# Revit family: Centralini_in_lamiera_Bticino_da_incasso_porta_piena
name_source: partatom
category: Equipement électrique
revit_build: Autodesk Revit 2018 (Build: 20170223_1515(x64)
units: mm (PartAtom-declared; Revit-internal decimal feet)

## family parameters
Basée sur le plan de construction = Non
Configuration du panneau = Deux colonnes, circuits au sein
Cote de connecteur circulaire = Utiliser le diamètre
Couper avec des vides une fois chargée = Non
Numéro OmniClass = 23.80.30.11.17
Partagée = Non
Point de calcul de pièce = Non
Titre OmniClass = Distribution Boards and Control Panels
Toujours verticalement = Oui
Type d'élément = Tableau de raccordement

## types (6) — shared parameters
Colore = RAL 7035
Condizioni Generali di Utilizzo = https://export.legrand.com
Fabricant = bticino
IK = 08
IP = 30
URL = www.bticino.com
materia = metallo

## per-type parameters (varying)
| type | Altezza da incasso | E209P/12D | E209P/24D | E209P/36D | E209P/54D | E209P/72D | E209P/96D | Larghezza incasso | altezza | larghezza | profondità |
| Centralini per terziaro Bticino E209P/12D | 310 mm  [stored 1.01706 ft] | Oui | Non | Non | Non | Non | Non | 310 mm  [stored 1.01706 ft] | 340 mm  [stored 1.11549 ft] | 340 mm  [stored 1.11549 ft] | 90 mm  [stored 0.295276 ft] |
| Centralini per terziaro Bticino E209P/24D | 435 mm  [stored 1.42717 ft] | Non | Oui | Non | Non | Non | Non | 310 mm  [stored 1.01706 ft] | 465 mm  [stored 1.52559 ft] | 340 mm  [stored 1.11549 ft] | 90 mm  [stored 0.295276 ft] |
| Centralini per terziaro Bticino E209P/36D | 560 mm  [stored 1.83727 ft] | Non | Non | Oui | Non | Non | Non | 310 mm  [stored 1.01706 ft] | 590 mm  [stored 1.9357 ft] | 340 mm  [stored 1.11549 ft] | 90 mm  [stored 0.295276 ft] |
| Centralini per terziaro Bticino E209P/54D | 670 mm  [stored 2.19816 ft] | Non | Non | Non | Oui | Non | Non | 460 mm  [stored 1.50919 ft] | 710 mm | 500 mm  [stored 1.64042 ft] | 119 mm  [stored 0.39042 ft] |
| Centralini per terziaro Bticino E209P/72D | 670 mm  [stored 2.19816 ft] | Non | Non | Non | Non | Oui | Non | 620 mm  [stored 2.03412 ft] | 710 mm | 660 mm  [stored 2.16535 ft] | 119 mm  [stored 0.39042 ft] |
| Centralini per terziaro Bticino E209P/96D | 820 mm  [stored 2.69029 ft] | Non | Non | Non | Non | Non | Oui | 620 mm  [stored 2.03412 ft] | 860 mm | 660 mm  [stored 2.16535 ft] | 119 mm  [stored 0.39042 ft] |

note: [stored X ft] marks values corroborated as IEEE doubles in the binary element streams (Revit-internal decimal feet)
